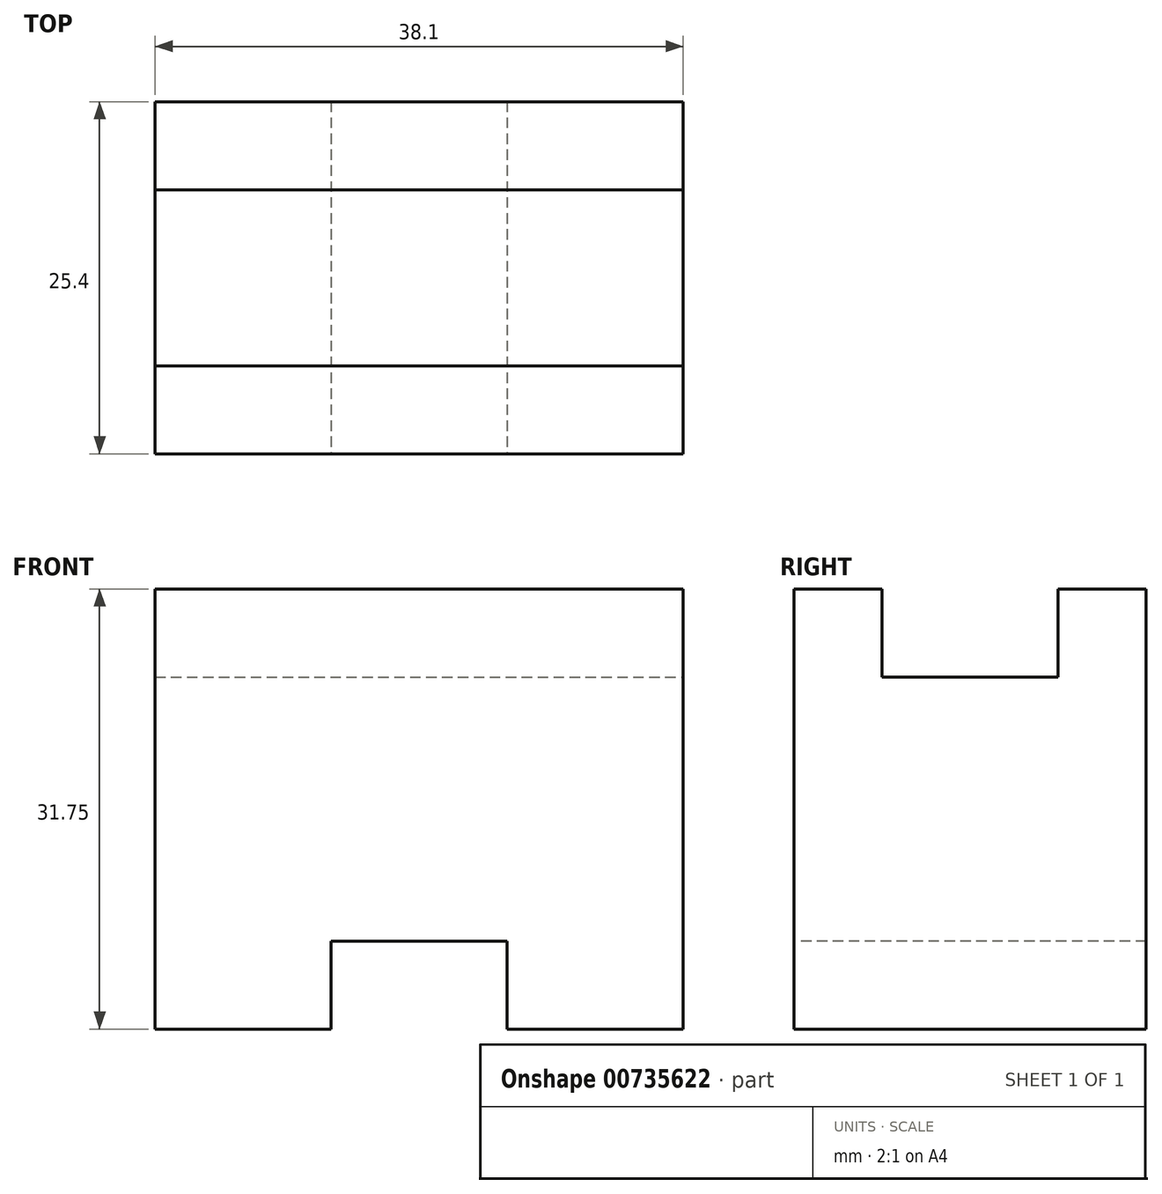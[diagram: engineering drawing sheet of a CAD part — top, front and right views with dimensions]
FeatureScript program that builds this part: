
annotation { "Feature Type Name" : "Feature", "Feature Type Description" : "" }
export const myFeature = defineFeature(function(context is Context, id is Id, definition is map)
    precondition{}
    {
        {
            var Q0;
            Q0=qCreatedBy(makeId("Right.planeOp"),FACE);
            var sketch = newSketch(context, id + "F0", { "sketchPlane" : qUnion([Q0])});
            skLineSegment(sketch, "E0.bottom", {"start": v(0, 0) * mm, "end": v(25.4, 0) * mm});
            skLineSegment(sketch, "E0.top", {"start": v(0, 31.75) * mm, "end": v(25.4, 31.75) * mm});
            skLineSegment(sketch, "E0.left", {"start": v(0, 0) * mm, "end": v(0, 31.75) * mm});
            skLineSegment(sketch, "E0.right", {"start": v(25.4, 0) * mm, "end": v(25.4, 31.75) * mm});
            skSolve(sketch);
        }
        {
            var Q0;
            Q0=makeQuery(id+"F0.imprint","IMPRINT",FACE,{"disambiguationData":[TD([[makeQuery(id+"F0.imprint","IMPRINT",EDGE,{"derivedFrom":sQuery(id+"F0.wireOp",EDGE,"E0.bottom")}),1.0]])]});
            extrude(context, id + "F1", {"entities" : qUnion([Q0]), "depth" : 38.1 * mm, "offsetDistance" : 25.4 * mm});
        }
        {
            var Q0;
            Q0=makeQuery(id+"F1.opExtrude","SWEPT_FACE",FACE,{"disambiguationData":[OSD([sQuery(id+"F0.wireOp",EDGE,"E0.left")])]});
            var sketch = newSketch(context, id + "F2", { "sketchPlane" : qUnion([Q0])});
            skLineSegment(sketch, "E1.bottom", {"start": v(12.7, 0) * mm, "end": v(25.4, 0) * mm});
            skLineSegment(sketch, "E1.top", {"start": v(12.7, 6.35) * mm, "end": v(25.4, 6.35) * mm});
            skLineSegment(sketch, "E1.left", {"start": v(12.7, 0) * mm, "end": v(12.7, 6.35) * mm});
            skLineSegment(sketch, "E1.right", {"start": v(25.4, 0) * mm, "end": v(25.4, 6.35) * mm});
            skSolve(sketch);
        }
        {
            var Q0;
            Q0=makeQuery(id+"F2.imprint","IMPRINT",FACE,{"disambiguationData":[TD([[makeQuery(id+"F2.imprint","IMPRINT",EDGE,{"derivedFrom":sQuery(id+"F2.wireOp",EDGE,"E1.bottom")}),-1.0]])]});
            extrude(context, id + "F3", {"entities" : qUnion([Q0]), "operationType" : NewBodyOperationType.REMOVE, "oppositeDirection" : true, "depth" : 25.4 * mm, "offsetDistance" : 25.4 * mm});
        }
        {
            var Q0;
            Q0=makeQuery(id+"F1.opExtrude","CAP_FACE",FACE,{"disambiguationData":[OSD([sQuery(id+"F0.wireOp",EDGE,"E0.bottom"),sQuery(id+"F0.wireOp",EDGE,"E0.top"),sQuery(id+"F0.wireOp",EDGE,"E0.left"),sQuery(id+"F0.wireOp",EDGE,"E0.right")])],"isStart":false});
            var sketch = newSketch(context, id + "F4", { "sketchPlane" : qUnion([Q0])});
            skLineSegment(sketch, "E2.bottom", {"start": v(6.35, 31.75) * mm, "end": v(19.05, 31.75) * mm});
            skLineSegment(sketch, "E2.top", {"start": v(6.35, 25.4) * mm, "end": v(19.05, 25.4) * mm});
            skLineSegment(sketch, "E2.left", {"start": v(6.35, 31.75) * mm, "end": v(6.35, 25.4) * mm});
            skLineSegment(sketch, "E2.right", {"start": v(19.05, 31.75) * mm, "end": v(19.05, 25.4) * mm});
            skSolve(sketch);
        }
        {
            var Q0;
            Q0=makeQuery(id+"F4.imprint","IMPRINT",FACE,{"disambiguationData":[TD([[makeQuery(id+"F4.imprint","IMPRINT",EDGE,{"derivedFrom":sQuery(id+"F4.wireOp",EDGE,"E2.bottom")}),-1.0]])]});
            extrude(context, id + "F5", {"entities" : qUnion([Q0]), "operationType" : NewBodyOperationType.REMOVE, "oppositeDirection" : true, "depth" : 50.8 * mm, "offsetDistance" : 25.4 * mm});
        }
    });
